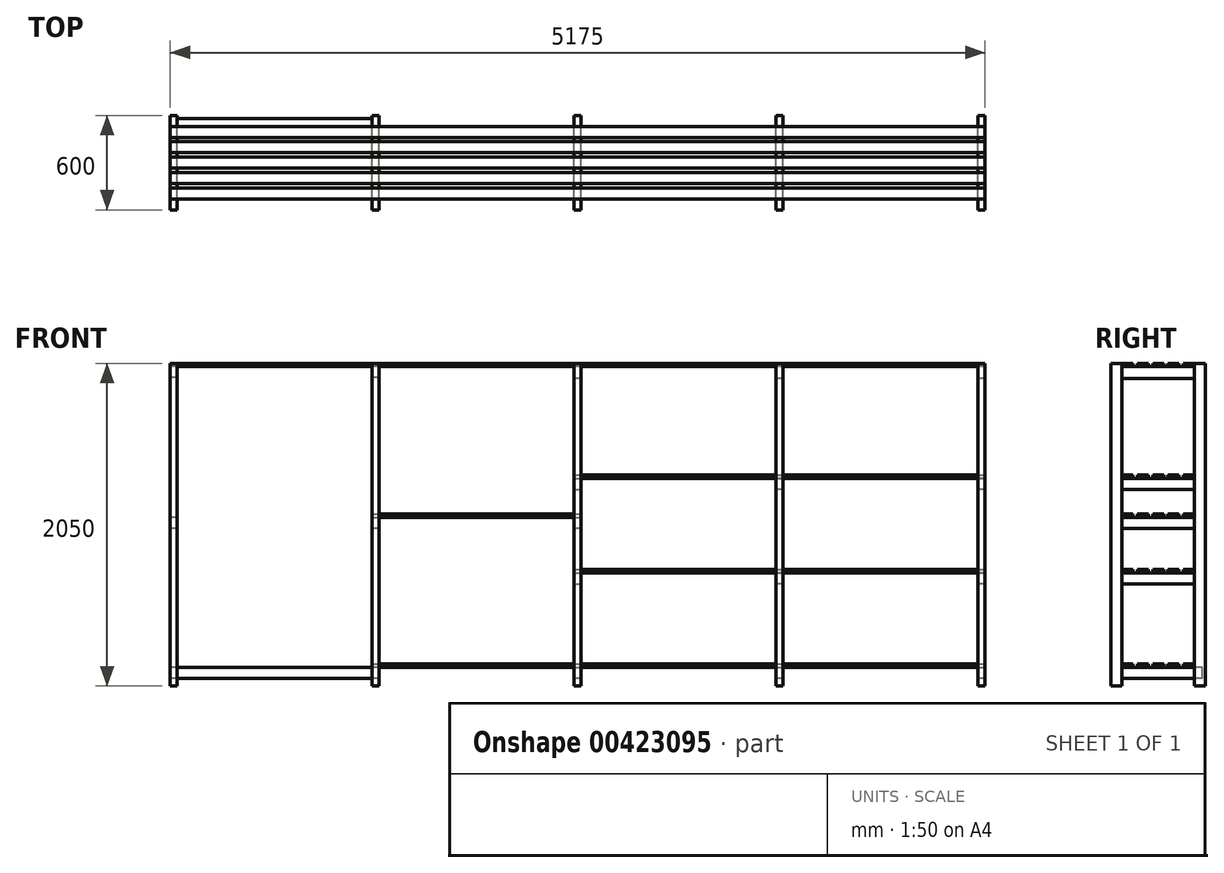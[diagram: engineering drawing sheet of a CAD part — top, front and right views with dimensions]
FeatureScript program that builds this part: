
annotation { "Feature Type Name" : "Feature", "Feature Type Description" : "" }
export const myFeature = defineFeature(function(context is Context, id is Id, definition is map)
    precondition{}
    {
        {
            var Q0;
            Q0=qCreatedBy(makeId("Top.planeOp"),FACE);
            var sketch = newSketch(context, id + "F0", { "sketchPlane" : qUnion([Q0])});
            skLineSegment(sketch, "E0.bottom", {"start": v(0, 0) * mm, "end": v(45, 0) * mm});
            skLineSegment(sketch, "E0.top", {"start": v(0, -70) * mm, "end": v(45, -70) * mm});
            skLineSegment(sketch, "E0.left", {"start": v(0, 0) * mm, "end": v(0, -70) * mm});
            skLineSegment(sketch, "E0.right", {"start": v(45, 0) * mm, "end": v(45, -70) * mm});
            skLineSegment(sketch, "E1.bottom", {"start": v(0, -530) * mm, "end": v(45, -530) * mm});
            skLineSegment(sketch, "E1.top", {"start": v(0, -600) * mm, "end": v(45, -600) * mm});
            skLineSegment(sketch, "E1.left", {"start": v(0, -530) * mm, "end": v(0, -600) * mm});
            skLineSegment(sketch, "E1.right", {"start": v(45, -530) * mm, "end": v(45, -600) * mm});
            skLineSegment(sketch, "E2.1.0.0", {"start": v(1282.5, -600) * mm, "end": v(1327.5, -600) * mm});
            skLineSegment(sketch, "E2.1.0.1", {"start": v(1282.5, -530) * mm, "end": v(1327.5, -530) * mm});
            skLineSegment(sketch, "E2.1.0.2", {"start": v(1327.5, 0) * mm, "end": v(1327.5, -70) * mm});
            skLineSegment(sketch, "E2.1.0.3", {"start": v(1282.5, 0) * mm, "end": v(1282.5, -70) * mm});
            skLineSegment(sketch, "E2.1.0.4", {"start": v(1282.5, -70) * mm, "end": v(1327.5, -70) * mm});
            skLineSegment(sketch, "E2.1.0.5", {"start": v(1282.5, 0) * mm, "end": v(1327.5, 0) * mm});
            skLineSegment(sketch, "E2.1.0.6", {"start": v(1282.5, -530) * mm, "end": v(1282.5, -600) * mm});
            skLineSegment(sketch, "E2.1.0.7", {"start": v(1327.5, -530) * mm, "end": v(1327.5, -600) * mm});
            skLineSegment(sketch, "E2.2.0.0", {"start": v(2565, -600) * mm, "end": v(2610, -600) * mm});
            skLineSegment(sketch, "E2.2.0.1", {"start": v(2565, -530) * mm, "end": v(2610, -530) * mm});
            skLineSegment(sketch, "E2.2.0.2", {"start": v(2610, 0) * mm, "end": v(2610, -70) * mm});
            skLineSegment(sketch, "E2.2.0.3", {"start": v(2565, 0) * mm, "end": v(2565, -70) * mm});
            skLineSegment(sketch, "E2.2.0.4", {"start": v(2565, -70) * mm, "end": v(2610, -70) * mm});
            skLineSegment(sketch, "E2.2.0.5", {"start": v(2565, 0) * mm, "end": v(2610, 0) * mm});
            skLineSegment(sketch, "E2.2.0.6", {"start": v(2565, -530) * mm, "end": v(2565, -600) * mm});
            skLineSegment(sketch, "E2.2.0.7", {"start": v(2610, -530) * mm, "end": v(2610, -600) * mm});
            skLineSegment(sketch, "E2.direction1", {"start": v(0, -600) * mm, "end": v(1282.5, -600) * mm, "construction": true});
            skLineSegment(sketch, "E3.0.3.0", {"start": v(3847.5, -600) * mm, "end": v(3892.5, -600) * mm});
            skLineSegment(sketch, "E3.3.3.0", {"start": v(3847.5, -530) * mm, "end": v(3892.5, -530) * mm});
            skLineSegment(sketch, "E3.6.3.0", {"start": v(3892.5, 0) * mm, "end": v(3892.5, -70) * mm});
            skLineSegment(sketch, "E3.9.3.0", {"start": v(3847.5, 0) * mm, "end": v(3847.5, -70) * mm});
            skLineSegment(sketch, "E3.12.3.0", {"start": v(3847.5, -70) * mm, "end": v(3892.5, -70) * mm});
            skLineSegment(sketch, "E3.15.3.0", {"start": v(3847.5, 0) * mm, "end": v(3892.5, 0) * mm});
            skLineSegment(sketch, "E3.18.3.0", {"start": v(3847.5, -530) * mm, "end": v(3847.5, -600) * mm});
            skLineSegment(sketch, "E3.21.3.0", {"start": v(3892.5, -530) * mm, "end": v(3892.5, -600) * mm});
            skLineSegment(sketch, "E4.0.4.0", {"start": v(5130, -600) * mm, "end": v(5175, -600) * mm});
            skLineSegment(sketch, "E4.3.4.0", {"start": v(5130, -530) * mm, "end": v(5175, -530) * mm});
            skLineSegment(sketch, "E4.6.4.0", {"start": v(5175, 0) * mm, "end": v(5175, -70) * mm});
            skLineSegment(sketch, "E4.9.4.0", {"start": v(5130, 0) * mm, "end": v(5130, -70) * mm});
            skLineSegment(sketch, "E4.12.4.0", {"start": v(5130, -70) * mm, "end": v(5175, -70) * mm});
            skLineSegment(sketch, "E4.15.4.0", {"start": v(5130, 0) * mm, "end": v(5175, 0) * mm});
            skLineSegment(sketch, "E4.18.4.0", {"start": v(5130, -530) * mm, "end": v(5130, -600) * mm});
            skLineSegment(sketch, "E4.21.4.0", {"start": v(5175, -530) * mm, "end": v(5175, -600) * mm});
            skSolve(sketch);
        }
        {
            var Q0;
            Q0 = qSketchRegion(id + "F0", true);
            extrude(context, id + "F1", {"entities" : qUnion([Q0]), "depth" : 2050 * mm});
        }
        {
            var Q0;
            Q0=makeQuery(id+"F1.opExtrude","SWEPT_FACE",FACE,{"disambiguationData":[OSD([sQuery(id+"F0.wireOp",EDGE,"E0.top")])]});
            var sketch = newSketch(context, id + "F2", { "sketchPlane" : qUnion([Q0])});
            skLineSegment(sketch, "E5.bottom", {"start": v(0, 2030) * mm, "end": v(45, 2030) * mm});
            skLineSegment(sketch, "E5.top", {"start": v(0, 1960) * mm, "end": v(45, 1960) * mm});
            skLineSegment(sketch, "E5.left", {"start": v(0, 2030) * mm, "end": v(0, 1960) * mm});
            skLineSegment(sketch, "E5.right", {"start": v(45, 2030) * mm, "end": v(45, 1960) * mm});
            skLineSegment(sketch, "E6.1.0.0", {"start": v(1282.5, 2030) * mm, "end": v(1282.5, 1960) * mm});
            skLineSegment(sketch, "E6.1.0.1", {"start": v(1327.5, 2030) * mm, "end": v(1327.5, 1960) * mm});
            skLineSegment(sketch, "E6.1.0.2", {"start": v(1282.5, 1960) * mm, "end": v(1327.5, 1960) * mm});
            skLineSegment(sketch, "E6.1.0.3", {"start": v(1282.5, 2030) * mm, "end": v(1327.5, 2030) * mm});
            skLineSegment(sketch, "E6.2.0.0", {"start": v(2565, 2030) * mm, "end": v(2565, 1955) * mm});
            skLineSegment(sketch, "E6.2.0.1", {"start": v(2610, 2030) * mm, "end": v(2610, 1955) * mm});
            skLineSegment(sketch, "E6.2.0.2", {"start": v(2565, 1955) * mm, "end": v(2610, 1955) * mm});
            skLineSegment(sketch, "E6.2.0.3", {"start": v(2565, 2030) * mm, "end": v(2610, 2030) * mm});
            skLineSegment(sketch, "E6.3.0.0", {"start": v(3847.5, 2030) * mm, "end": v(3847.5, 1955) * mm});
            skLineSegment(sketch, "E6.3.0.1", {"start": v(3892.5, 2030) * mm, "end": v(3892.5, 1955) * mm});
            skLineSegment(sketch, "E6.3.0.2", {"start": v(3847.5, 1955) * mm, "end": v(3892.5, 1955) * mm});
            skLineSegment(sketch, "E6.3.0.3", {"start": v(3847.5, 2030) * mm, "end": v(3892.5, 2030) * mm});
            skLineSegment(sketch, "E6.4.0.0", {"start": v(5130, 2030) * mm, "end": v(5130, 1955) * mm});
            skLineSegment(sketch, "E6.4.0.1", {"start": v(5175, 2030) * mm, "end": v(5175, 1955) * mm});
            skLineSegment(sketch, "E6.4.0.2", {"start": v(5130, 1955) * mm, "end": v(5175, 1955) * mm});
            skLineSegment(sketch, "E6.4.0.3", {"start": v(5130, 2030) * mm, "end": v(5175, 2030) * mm});
            skLineSegment(sketch, "E6.direction1", {"start": v(0, 1960) * mm, "end": v(1282.5, 1960) * mm, "construction": true});
            skLineSegment(sketch, "E7.bottom", {"start": v(0, 50) * mm, "end": v(45, 50) * mm});
            skLineSegment(sketch, "E7.top", {"start": v(0, 120) * mm, "end": v(45, 120) * mm});
            skLineSegment(sketch, "E7.left", {"start": v(0, 50) * mm, "end": v(0, 120) * mm});
            skLineSegment(sketch, "E7.right", {"start": v(45, 50) * mm, "end": v(45, 120) * mm});
            skLineSegment(sketch, "E8.1.0.0", {"start": v(1282.5, 120) * mm, "end": v(1327.5, 120) * mm});
            skLineSegment(sketch, "E8.1.0.1", {"start": v(1327.5, 50) * mm, "end": v(1327.5, 120) * mm});
            skLineSegment(sketch, "E8.1.0.2", {"start": v(1282.5, 50) * mm, "end": v(1327.5, 50) * mm});
            skLineSegment(sketch, "E8.1.0.3", {"start": v(1282.5, 50) * mm, "end": v(1282.5, 120) * mm});
            skLineSegment(sketch, "E8.2.0.0", {"start": v(2565, 120) * mm, "end": v(2610, 120) * mm});
            skLineSegment(sketch, "E8.2.0.1", {"start": v(2610, 50) * mm, "end": v(2610, 120) * mm});
            skLineSegment(sketch, "E8.2.0.2", {"start": v(2565, 50) * mm, "end": v(2610, 50) * mm});
            skLineSegment(sketch, "E8.2.0.3", {"start": v(2565, 50) * mm, "end": v(2565, 120) * mm});
            skLineSegment(sketch, "E8.3.0.0", {"start": v(3847.5, 120) * mm, "end": v(3892.5, 120) * mm});
            skLineSegment(sketch, "E8.3.0.1", {"start": v(3892.5, 50) * mm, "end": v(3892.5, 120) * mm});
            skLineSegment(sketch, "E8.3.0.2", {"start": v(3847.5, 50) * mm, "end": v(3892.5, 50) * mm});
            skLineSegment(sketch, "E8.3.0.3", {"start": v(3847.5, 50) * mm, "end": v(3847.5, 120) * mm});
            skLineSegment(sketch, "E8.4.0.0", {"start": v(5130, 120) * mm, "end": v(5175, 120) * mm});
            skLineSegment(sketch, "E8.4.0.1", {"start": v(5175, 50) * mm, "end": v(5175, 120) * mm});
            skLineSegment(sketch, "E8.4.0.2", {"start": v(5130, 50) * mm, "end": v(5175, 50) * mm});
            skLineSegment(sketch, "E8.4.0.3", {"start": v(5130, 50) * mm, "end": v(5130, 120) * mm});
            skLineSegment(sketch, "E8.direction1", {"start": v(0, 50) * mm, "end": v(1282.5, 50) * mm, "construction": true});
            skLineSegment(sketch, "E9.bottom", {"start": v(5130, 650) * mm, "end": v(5175, 650) * mm});
            skLineSegment(sketch, "E9.top", {"start": v(5130, 720) * mm, "end": v(5175, 720) * mm});
            skLineSegment(sketch, "E9.left", {"start": v(5130, 650) * mm, "end": v(5130, 720) * mm});
            skLineSegment(sketch, "E9.right", {"start": v(5175, 650) * mm, "end": v(5175, 720) * mm});
            skLineSegment(sketch, "E10.bottom", {"start": v(5130, 1250) * mm, "end": v(5175, 1250) * mm});
            skLineSegment(sketch, "E10.top", {"start": v(5130, 1320) * mm, "end": v(5175, 1320) * mm});
            skLineSegment(sketch, "E10.left", {"start": v(5130, 1250) * mm, "end": v(5130, 1320) * mm});
            skLineSegment(sketch, "E10.right", {"start": v(5175, 1250) * mm, "end": v(5175, 1320) * mm});
            skLineSegment(sketch, "E11.bottom", {"start": v(3847.5, 650) * mm, "end": v(3892.5, 650) * mm});
            skLineSegment(sketch, "E11.top", {"start": v(3847.5, 720) * mm, "end": v(3892.5, 720) * mm});
            skLineSegment(sketch, "E11.left", {"start": v(3847.5, 650) * mm, "end": v(3847.5, 720) * mm});
            skLineSegment(sketch, "E11.right", {"start": v(3892.5, 650) * mm, "end": v(3892.5, 720) * mm});
            skLineSegment(sketch, "E12.bottom", {"start": v(3847.5, 1250) * mm, "end": v(3892.5, 1250) * mm});
            skLineSegment(sketch, "E12.top", {"start": v(3847.5, 1320) * mm, "end": v(3892.5, 1320) * mm});
            skLineSegment(sketch, "E12.left", {"start": v(3847.5, 1250) * mm, "end": v(3847.5, 1320) * mm});
            skLineSegment(sketch, "E12.right", {"start": v(3892.5, 1250) * mm, "end": v(3892.5, 1320) * mm});
            skLineSegment(sketch, "E13.bottom", {"start": v(2610, 1320) * mm, "end": v(2565, 1320) * mm});
            skLineSegment(sketch, "E13.top", {"start": v(2610, 1250) * mm, "end": v(2565, 1250) * mm});
            skLineSegment(sketch, "E13.left", {"start": v(2610, 1320) * mm, "end": v(2610, 1250) * mm});
            skLineSegment(sketch, "E13.right", {"start": v(2565, 1320) * mm, "end": v(2565, 1250) * mm});
            skLineSegment(sketch, "E14.bottom", {"start": v(2610, 650) * mm, "end": v(2565, 650) * mm});
            skLineSegment(sketch, "E14.top", {"start": v(2610, 720) * mm, "end": v(2565, 720) * mm});
            skLineSegment(sketch, "E14.left", {"start": v(2610, 650) * mm, "end": v(2610, 720) * mm});
            skLineSegment(sketch, "E14.right", {"start": v(2565, 650) * mm, "end": v(2565, 720) * mm});
            skLineSegment(sketch, "E15.bottom", {"start": v(0, 1070) * mm, "end": v(45, 1070) * mm});
            skLineSegment(sketch, "E15.top", {"start": v(0, 1000) * mm, "end": v(45, 1000) * mm});
            skLineSegment(sketch, "E15.left", {"start": v(0, 1070) * mm, "end": v(0, 1000) * mm});
            skLineSegment(sketch, "E15.right", {"start": v(45, 1070) * mm, "end": v(45, 1000) * mm});
            skLineSegment(sketch, "E16.1.0.0", {"start": v(1282.5, 1070) * mm, "end": v(1327.5, 1070) * mm});
            skLineSegment(sketch, "E16.1.0.1", {"start": v(1327.5, 1070) * mm, "end": v(1327.5, 1000) * mm});
            skLineSegment(sketch, "E16.1.0.2", {"start": v(1282.5, 1000) * mm, "end": v(1327.5, 1000) * mm});
            skLineSegment(sketch, "E16.1.0.3", {"start": v(1282.5, 1070) * mm, "end": v(1282.5, 1000) * mm});
            skLineSegment(sketch, "E16.2.0.0", {"start": v(2565, 1070) * mm, "end": v(2610, 1070) * mm});
            skLineSegment(sketch, "E16.2.0.1", {"start": v(2610, 1070) * mm, "end": v(2610, 1000) * mm});
            skLineSegment(sketch, "E16.2.0.2", {"start": v(2565, 1000) * mm, "end": v(2610, 1000) * mm});
            skLineSegment(sketch, "E16.2.0.3", {"start": v(2565, 1070) * mm, "end": v(2565, 1000) * mm});
            skLineSegment(sketch, "E16.direction1", {"start": v(0, 1000) * mm, "end": v(1282.5, 1000) * mm, "construction": true});
            skSolve(sketch);
        }
        {
            var Q0;
            Q0 = qSketchRegion(id + "F2", true);
            var Q1;
            Q1=makeQuery(id+"F1.opExtrude","SWEPT_FACE",FACE,{"disambiguationData":[OSD([sQuery(id+"F0.wireOp",EDGE,"E4.3.4.0")])]});
            extrude(context, id + "F3", {"entities" : qUnion([Q0]), "endBound" : BoundingType.UP_TO_SURFACE, "endBoundEntityFace" : qUnion([Q1]), "depth" : 25 * mm});
        }
        {
            var Q0;
            Q0=makeQuery(id+"F1.opExtrude","SWEPT_FACE",FACE,{"disambiguationData":[OSD([sQuery(id+"F0.wireOp",EDGE,"E0.left")])]});
            var sketch = newSketch(context, id + "F4", { "sketchPlane" : qUnion([Q0])});
            skLineSegment(sketch, "E17.bottom", {"start": v(530, 2030) * mm, "end": v(460, 2030) * mm});
            skLineSegment(sketch, "E17.top", {"start": v(530, 2050) * mm, "end": v(460, 2050) * mm});
            skLineSegment(sketch, "E17.left", {"start": v(530, 2030) * mm, "end": v(530, 2050) * mm});
            skLineSegment(sketch, "E17.right", {"start": v(460, 2030) * mm, "end": v(460, 2050) * mm});
            skLineSegment(sketch, "E18.bottom", {"start": v(70, 2050) * mm, "end": v(140, 2050) * mm});
            skLineSegment(sketch, "E18.top", {"start": v(70, 2030) * mm, "end": v(140, 2030) * mm});
            skLineSegment(sketch, "E18.left", {"start": v(70, 2050) * mm, "end": v(70, 2030) * mm});
            skLineSegment(sketch, "E18.right", {"start": v(140, 2050) * mm, "end": v(140, 2030) * mm});
            skLineSegment(sketch, "E19.bottom", {"start": v(237.5, 2050) * mm, "end": v(167.5, 2050) * mm});
            skLineSegment(sketch, "E19.top", {"start": v(237.5, 2030) * mm, "end": v(167.5, 2030) * mm});
            skLineSegment(sketch, "E19.left", {"start": v(237.5, 2050) * mm, "end": v(237.5, 2030) * mm});
            skLineSegment(sketch, "E19.right", {"start": v(167.5, 2050) * mm, "end": v(167.5, 2030) * mm});
            skLineSegment(sketch, "E20.bottom", {"start": v(265, 2050) * mm, "end": v(335, 2050) * mm});
            skLineSegment(sketch, "E20.top", {"start": v(265, 2030) * mm, "end": v(335, 2030) * mm});
            skLineSegment(sketch, "E20.left", {"start": v(265, 2050) * mm, "end": v(265, 2030) * mm});
            skLineSegment(sketch, "E20.right", {"start": v(335, 2050) * mm, "end": v(335, 2030) * mm});
            skLineSegment(sketch, "E21", {"start": v(265, 2050) * mm, "end": v(237.5, 2050) * mm, "construction": true});
            skLineSegment(sketch, "E22", {"start": v(167.5, 2050) * mm, "end": v(140, 2050) * mm, "construction": true});
            skLineSegment(sketch, "E23.bottom", {"start": v(432.5, 2050) * mm, "end": v(362.5, 2050) * mm});
            skLineSegment(sketch, "E23.top", {"start": v(432.5, 2030) * mm, "end": v(362.5, 2030) * mm});
            skLineSegment(sketch, "E23.left", {"start": v(432.5, 2050) * mm, "end": v(432.5, 2030) * mm});
            skLineSegment(sketch, "E23.right", {"start": v(362.5, 2050) * mm, "end": v(362.5, 2030) * mm});
            skLineSegment(sketch, "E24", {"start": v(335, 2050) * mm, "end": v(362.5, 2050) * mm, "construction": true});
            skLineSegment(sketch, "E25", {"start": v(432.5, 2050) * mm, "end": v(460, 2050) * mm, "construction": true});
            skSolve(sketch);
        }
        {
            var Q0;
            Q0 = qSketchRegion(id + "F4", true);
            var Q1;
            Q1=makeQuery(id+"F3.opExtrude","SWEPT_FACE",FACE,{"disambiguationData":[OSD([sQuery(id+"F2.wireOp",EDGE,"E6.4.0.1")])]});
            extrude(context, id + "F5", {"entities" : qUnion([Q0]), "endBound" : BoundingType.UP_TO_SURFACE, "oppositeDirection" : true, "endBoundEntityFace" : qUnion([Q1]), "depth" : 25 * mm});
        }
        {
            var Q0;
            Q0=makeQuery(id+"F3.opExtrude","SWEPT_FACE",FACE,{"disambiguationData":[OSD([sQuery(id+"F2.wireOp",EDGE,"E10.right")])]});
            var sketch = newSketch(context, id + "F6", { "sketchPlane" : qUnion([Q0])});
            skLineSegment(sketch, "E26.bottom", {"start": v(-530, 1320) * mm, "end": v(-460, 1320) * mm});
            skLineSegment(sketch, "E26.top", {"start": v(-530, 1340) * mm, "end": v(-460, 1340) * mm});
            skLineSegment(sketch, "E26.left", {"start": v(-530, 1320) * mm, "end": v(-530, 1340) * mm});
            skLineSegment(sketch, "E26.right", {"start": v(-460, 1320) * mm, "end": v(-460, 1340) * mm});
            skLineSegment(sketch, "E27.bottom", {"start": v(-335, 1320) * mm, "end": v(-265, 1320) * mm});
            skLineSegment(sketch, "E27.top", {"start": v(-335, 1340) * mm, "end": v(-265, 1340) * mm});
            skLineSegment(sketch, "E27.left", {"start": v(-335, 1320) * mm, "end": v(-335, 1340) * mm});
            skLineSegment(sketch, "E27.right", {"start": v(-265, 1320) * mm, "end": v(-265, 1340) * mm});
            skLineSegment(sketch, "E28.bottom", {"start": v(-237.5, 1320) * mm, "end": v(-167.5, 1320) * mm});
            skLineSegment(sketch, "E28.top", {"start": v(-237.5, 1340) * mm, "end": v(-167.5, 1340) * mm});
            skLineSegment(sketch, "E28.left", {"start": v(-237.5, 1320) * mm, "end": v(-237.5, 1340) * mm});
            skLineSegment(sketch, "E28.right", {"start": v(-167.5, 1320) * mm, "end": v(-167.5, 1340) * mm});
            skLineSegment(sketch, "E29.bottom", {"start": v(-140, 1320) * mm, "end": v(-70, 1320) * mm});
            skLineSegment(sketch, "E29.top", {"start": v(-140, 1340) * mm, "end": v(-70, 1340) * mm});
            skLineSegment(sketch, "E29.left", {"start": v(-140, 1320) * mm, "end": v(-140, 1340) * mm});
            skLineSegment(sketch, "E29.right", {"start": v(-70, 1320) * mm, "end": v(-70, 1340) * mm});
            skLineSegment(sketch, "E30.0.1.0", {"start": v(-335, 720) * mm, "end": v(-265, 720) * mm});
            skLineSegment(sketch, "E30.0.1.1", {"start": v(-335, 740) * mm, "end": v(-265, 740) * mm});
            skLineSegment(sketch, "E30.0.1.2", {"start": v(-432.5, 740) * mm, "end": v(-362.5, 740) * mm});
            skLineSegment(sketch, "E30.0.1.3", {"start": v(-432.5, 720) * mm, "end": v(-362.5, 720) * mm});
            skLineSegment(sketch, "E30.0.1.4", {"start": v(-530, 740) * mm, "end": v(-460, 740) * mm});
            skLineSegment(sketch, "E30.0.1.5", {"start": v(-237.5, 720) * mm, "end": v(-167.5, 720) * mm});
            skLineSegment(sketch, "E30.0.1.6", {"start": v(-530, 720) * mm, "end": v(-460, 720) * mm});
            skLineSegment(sketch, "E30.0.1.7", {"start": v(-237.5, 740) * mm, "end": v(-167.5, 740) * mm});
            skLineSegment(sketch, "E30.0.1.8", {"start": v(-432.5, 720) * mm, "end": v(-432.5, 740) * mm});
            skLineSegment(sketch, "E30.0.1.9", {"start": v(-362.5, 720) * mm, "end": v(-362.5, 740) * mm});
            skLineSegment(sketch, "E30.0.1.10", {"start": v(-237.5, 720) * mm, "end": v(-237.5, 740) * mm});
            skLineSegment(sketch, "E30.0.1.11", {"start": v(-460, 720) * mm, "end": v(-460, 740) * mm});
            skLineSegment(sketch, "E30.0.1.12", {"start": v(-530, 720) * mm, "end": v(-530, 740) * mm});
            skLineSegment(sketch, "E30.0.1.13", {"start": v(-335, 720) * mm, "end": v(-335, 740) * mm});
            skLineSegment(sketch, "E30.0.1.14", {"start": v(-265, 720) * mm, "end": v(-265, 740) * mm});
            skLineSegment(sketch, "E30.0.1.15", {"start": v(-167.5, 720) * mm, "end": v(-167.5, 740) * mm});
            skLineSegment(sketch, "E30.0.2.0", {"start": v(-335, 120) * mm, "end": v(-265, 120) * mm});
            skLineSegment(sketch, "E30.0.2.1", {"start": v(-335, 140) * mm, "end": v(-265, 140) * mm});
            skLineSegment(sketch, "E30.0.2.2", {"start": v(-432.5, 140) * mm, "end": v(-362.5, 140) * mm});
            skLineSegment(sketch, "E30.0.2.3", {"start": v(-432.5, 120) * mm, "end": v(-362.5, 120) * mm});
            skLineSegment(sketch, "E30.0.2.4", {"start": v(-530, 140) * mm, "end": v(-460, 140) * mm});
            skLineSegment(sketch, "E30.0.2.5", {"start": v(-237.5, 120) * mm, "end": v(-167.5, 120) * mm});
            skLineSegment(sketch, "E30.0.2.6", {"start": v(-530, 120) * mm, "end": v(-460, 120) * mm});
            skLineSegment(sketch, "E30.0.2.7", {"start": v(-237.5, 140) * mm, "end": v(-167.5, 140) * mm});
            skLineSegment(sketch, "E30.0.2.8", {"start": v(-432.5, 120) * mm, "end": v(-432.5, 140) * mm});
            skLineSegment(sketch, "E30.0.2.9", {"start": v(-362.5, 120) * mm, "end": v(-362.5, 140) * mm});
            skLineSegment(sketch, "E30.0.2.10", {"start": v(-237.5, 120) * mm, "end": v(-237.5, 140) * mm});
            skLineSegment(sketch, "E30.0.2.11", {"start": v(-460, 120) * mm, "end": v(-460, 140) * mm});
            skLineSegment(sketch, "E30.0.2.12", {"start": v(-530, 120) * mm, "end": v(-530, 140) * mm});
            skLineSegment(sketch, "E30.0.2.13", {"start": v(-335, 120) * mm, "end": v(-335, 140) * mm});
            skLineSegment(sketch, "E30.0.2.14", {"start": v(-265, 120) * mm, "end": v(-265, 140) * mm});
            skLineSegment(sketch, "E30.0.2.15", {"start": v(-167.5, 120) * mm, "end": v(-167.5, 140) * mm});
            skLineSegment(sketch, "E30.direction2", {"start": v(-530, 1320) * mm, "end": v(-530, 720) * mm, "construction": true});
            skLineSegment(sketch, "E31.bottom", {"start": v(-432.5, 1340) * mm, "end": v(-362.5, 1340) * mm});
            skLineSegment(sketch, "E31.top", {"start": v(-432.5, 1320) * mm, "end": v(-362.5, 1320) * mm});
            skLineSegment(sketch, "E31.left", {"start": v(-432.5, 1340) * mm, "end": v(-432.5, 1320) * mm});
            skLineSegment(sketch, "E31.right", {"start": v(-362.5, 1340) * mm, "end": v(-362.5, 1320) * mm});
            skLineSegment(sketch, "E32.bottom", {"start": v(-70, 720) * mm, "end": v(-140, 720) * mm});
            skLineSegment(sketch, "E32.top", {"start": v(-70, 740) * mm, "end": v(-140, 740) * mm});
            skLineSegment(sketch, "E32.left", {"start": v(-70, 720) * mm, "end": v(-70, 740) * mm});
            skLineSegment(sketch, "E32.right", {"start": v(-140, 720) * mm, "end": v(-140, 740) * mm});
            skLineSegment(sketch, "E33.bottom", {"start": v(-70, 120) * mm, "end": v(-140, 120) * mm});
            skLineSegment(sketch, "E33.top", {"start": v(-70, 140) * mm, "end": v(-140, 140) * mm});
            skLineSegment(sketch, "E33.left", {"start": v(-70, 120) * mm, "end": v(-70, 140) * mm});
            skLineSegment(sketch, "E33.right", {"start": v(-140, 120) * mm, "end": v(-140, 140) * mm});
            skSolve(sketch);
        }
        {
            var Q0;
            Q0 = qSketchRegion(id + "F6", true);
            var Q1;
            Q1=makeQuery(id+"F3.opExtrude","SWEPT_FACE",FACE,{"disambiguationData":[OSD([sQuery(id+"F2.wireOp",EDGE,"E14.right")])]});
            extrude(context, id + "F7", {"entities" : qUnion([Q0]), "endBound" : BoundingType.UP_TO_SURFACE, "oppositeDirection" : true, "endBoundEntityFace" : qUnion([Q1]), "depth" : 25 * mm});
        }
        {
            var Q0;
            Q0=makeQuery(id+"F3.opExtrude","SWEPT_FACE",FACE,{"disambiguationData":[OSD([sQuery(id+"F2.wireOp",EDGE,"E16.2.0.1")])]});
            var sketch = newSketch(context, id + "F8", { "sketchPlane" : qUnion([Q0])});
            skLineSegment(sketch, "E34.bottom", {"start": v(-530, 1070) * mm, "end": v(-460, 1070) * mm});
            skLineSegment(sketch, "E34.top", {"start": v(-530, 1095) * mm, "end": v(-460, 1095) * mm});
            skLineSegment(sketch, "E34.left", {"start": v(-530, 1070) * mm, "end": v(-530, 1095) * mm});
            skLineSegment(sketch, "E34.right", {"start": v(-460, 1070) * mm, "end": v(-460, 1095) * mm});
            skLineSegment(sketch, "E35.bottom", {"start": v(-335, 1095) * mm, "end": v(-265, 1095) * mm});
            skLineSegment(sketch, "E35.top", {"start": v(-335, 1070) * mm, "end": v(-265, 1070) * mm});
            skLineSegment(sketch, "E35.left", {"start": v(-335, 1095) * mm, "end": v(-335, 1070) * mm});
            skLineSegment(sketch, "E35.right", {"start": v(-265, 1095) * mm, "end": v(-265, 1070) * mm});
            skLineSegment(sketch, "E36.bottom", {"start": v(-237.5, 1095) * mm, "end": v(-167.5, 1095) * mm});
            skLineSegment(sketch, "E36.top", {"start": v(-237.5, 1070) * mm, "end": v(-167.5, 1070) * mm});
            skLineSegment(sketch, "E36.left", {"start": v(-237.5, 1095) * mm, "end": v(-237.5, 1070) * mm});
            skLineSegment(sketch, "E36.right", {"start": v(-167.5, 1095) * mm, "end": v(-167.5, 1070) * mm});
            skLineSegment(sketch, "E37.bottom", {"start": v(-140, 1095) * mm, "end": v(-70, 1095) * mm});
            skLineSegment(sketch, "E37.top", {"start": v(-140, 1070) * mm, "end": v(-70, 1070) * mm});
            skLineSegment(sketch, "E37.left", {"start": v(-140, 1095) * mm, "end": v(-140, 1070) * mm});
            skLineSegment(sketch, "E37.right", {"start": v(-70, 1095) * mm, "end": v(-70, 1070) * mm});
            skLineSegment(sketch, "E38.bottom", {"start": v(-460, 140) * mm, "end": v(-530, 140) * mm});
            skLineSegment(sketch, "E38.top", {"start": v(-460, 120) * mm, "end": v(-530, 120) * mm});
            skLineSegment(sketch, "E38.left", {"start": v(-460, 140) * mm, "end": v(-460, 120) * mm});
            skLineSegment(sketch, "E38.right", {"start": v(-530, 140) * mm, "end": v(-530, 120) * mm});
            skLineSegment(sketch, "E39.bottom", {"start": v(-432.5, 140) * mm, "end": v(-362.5, 140) * mm});
            skLineSegment(sketch, "E39.top", {"start": v(-432.5, 120) * mm, "end": v(-362.5, 120) * mm});
            skLineSegment(sketch, "E39.left", {"start": v(-432.5, 140) * mm, "end": v(-432.5, 120) * mm});
            skLineSegment(sketch, "E39.right", {"start": v(-362.5, 140) * mm, "end": v(-362.5, 120) * mm});
            skLineSegment(sketch, "E40.bottom", {"start": v(-335, 140) * mm, "end": v(-265, 140) * mm});
            skLineSegment(sketch, "E40.top", {"start": v(-335, 120) * mm, "end": v(-265, 120) * mm});
            skLineSegment(sketch, "E40.left", {"start": v(-335, 140) * mm, "end": v(-335, 120) * mm});
            skLineSegment(sketch, "E40.right", {"start": v(-265, 140) * mm, "end": v(-265, 120) * mm});
            skLineSegment(sketch, "E41.bottom", {"start": v(-237.5, 120) * mm, "end": v(-167.5, 120) * mm});
            skLineSegment(sketch, "E41.top", {"start": v(-237.5, 140) * mm, "end": v(-167.5, 140) * mm});
            skLineSegment(sketch, "E41.left", {"start": v(-237.5, 120) * mm, "end": v(-237.5, 140) * mm});
            skLineSegment(sketch, "E41.right", {"start": v(-167.5, 120) * mm, "end": v(-167.5, 140) * mm});
            skLineSegment(sketch, "E42.bottom", {"start": v(-432.5, 1095) * mm, "end": v(-362.5, 1095) * mm});
            skLineSegment(sketch, "E42.top", {"start": v(-432.5, 1070) * mm, "end": v(-362.5, 1070) * mm});
            skLineSegment(sketch, "E42.left", {"start": v(-432.5, 1095) * mm, "end": v(-432.5, 1070) * mm});
            skLineSegment(sketch, "E42.right", {"start": v(-362.5, 1095) * mm, "end": v(-362.5, 1070) * mm});
            skSolve(sketch);
        }
        {
            var Q0;
            Q0 = qSketchRegion(id + "F8", true);
            var Q1;
            Q1=makeQuery(id+"F3.opExtrude","SWEPT_FACE",FACE,{"disambiguationData":[OSD([sQuery(id+"F2.wireOp",EDGE,"E16.1.0.3")])]});
            extrude(context, id + "F9", {"entities" : qUnion([Q0]), "endBound" : BoundingType.UP_TO_SURFACE, "oppositeDirection" : true, "endBoundEntityFace" : qUnion([Q1]), "depth" : 25 * mm});
        }
        {
            var Q0;
            Q0=makeQuery(id+"F1.opExtrude","SWEPT_FACE",FACE,{"disambiguationData":[OSD([sQuery(id+"F0.wireOp",EDGE,"E2.1.0.3")])]});
            var sketch = newSketch(context, id + "F10", { "sketchPlane" : qUnion([Q0])});
            skLineSegment(sketch, "E43.bottom", {"start": v(70, 120) * mm, "end": v(20, 120) * mm});
            skLineSegment(sketch, "E43.top", {"start": v(70, 50) * mm, "end": v(20, 50) * mm});
            skLineSegment(sketch, "E43.left", {"start": v(70, 120) * mm, "end": v(70, 50) * mm});
            skLineSegment(sketch, "E43.right", {"start": v(20, 120) * mm, "end": v(20, 50) * mm});
            skSolve(sketch);
        }
        {
            var Q0;
            Q0 = qSketchRegion(id + "F10", true);
            var Q1;
            Q1=makeQuery(id+"F1.opExtrude","SWEPT_FACE",FACE,{"disambiguationData":[OSD([sQuery(id+"F0.wireOp",EDGE,"E0.right")])]});
            extrude(context, id + "F11", {"entities" : qUnion([Q0]), "endBound" : BoundingType.UP_TO_SURFACE, "endBoundEntityFace" : qUnion([Q1]), "depth" : 25 * mm});
        }
    });
